# Revit family: Grinder_Package-Indoor-Zoeller-18x30-915-0005
name_source: partatom
category: Mechanical Equipment
revit_build: Autodesk Revit 2014 (Build: 20130308_1515(x64)
units: mm (PartAtom-declared; Revit-internal decimal feet)

## types (1)
- 915-0005/BN801/18x30/2V1.25D - 115V, 7Amps, 32gpm@5'
    Alarm = Yes
    Amps = 7
    Assembly Code = D2030400
    Basin Type = Poly molded basin with 2V1-1/4D simplex steel cover with 10-4012 alarm.
    CW Connection = Yes
    Cap = Engineered plastic
    Cord Length = 180"
    Cord Type = UL listed neoprene
    Cutter = Hardened stainless steel, Rockwell C40-50
    Default Elevation = 0"
    Description = 915 Grinder Package
    Diameter = 18"
    Discharge Radius = 5/8"
    Discharge Size = 1 1/4"
    Gasket = Closed cell tank gasket; Buna-N pump o-ring
    HW Connection = No
    Hardware = Stainless Steel
    Height = 30"
    Hertz = 60
    Horse Power = 1/2
    Impeller = Engineered plastic
    Impeller Type = Non-clogging vortex.
    Inlet Diameter = 4 1/2"
    Inlet Radius = 2 1/4"
    Manufacturer = Zoeller
    Material = Foam-Zoeller-Engineered plastic
    Max. Flow at Min. Head = 32 GPM (121 LPM)
    Max. Head = 26' (7.9 m)
    Max. Operating Temp. = 130°F (54°C)
    Mechanical Seals = Carbon/ceramic
    Model = 915-0005/BN801/18x30/2V1.25D
    Nominal Radius = 5"
    Off Point = 6 1/2"
    On Point = 13 3/8"
    Operation = Automatic
    Phase = 1
    Price = Prices may vary. Please consult Manufacturer Representative for most up-to-date price list.
    Product Documentation Link = http://cdn.qleapahead.com
    Product Page URL = http://www.zoellerpumps.com
    Pump Housing = Engineered Plastic
    RPM = 3450
    Radius = 9"
    Shipping Weight = 61.00 lb
    URL = http://www.zoeller.com
    Vent Connection = No
    Vent Connection Radius = 1"
    Voltage = 115 V
    Waste Connection = Yes

## geometry (parser evidence)
native form markers: Sweep x3
no freeform markers — native parametric forms only
